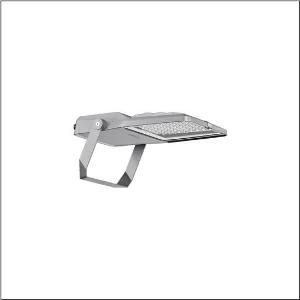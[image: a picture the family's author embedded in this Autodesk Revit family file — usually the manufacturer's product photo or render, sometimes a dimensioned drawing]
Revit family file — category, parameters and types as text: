
# Revit family: floodlight_fl_21_iq_mini___pl52_5xa7772c1d1a_38f0
name_source: partatom
category: Lighting Fixtures
units: mm (PartAtom-declared; Revit-internal decimal feet)

## family parameters
Cut with Voids When Loaded = No
Host = Face
Light Source = No
Part Type = Normal
Room Calculation Point = No
Round Connector Dimension = Use Diameter
Shared = No

## types (1)
- --- (1 x LED, 10110 lm, 87.2 W, 2200K)
    Apparent Load = 87 VA
    CIE Flux Codes = 26 60 98 100 100
    Color Rendering = 70
    Color Temperature = 2200K
    Default Elevation = 1800 mm
    Description = Floodlight FL 21 iQ mini, floodlight, primary light control with lens, of PMMA, primary optical cover: protective disc, of toughened safety glass, transparent, light distribution: PL52, light emission: direct distribution, installation type: surface-mounted, LED, High Power LED, rated luminous flux: 10.110lm, luminous efficacy: 116lm/W, light colour: 722, colour temperature: 2200K, control: Street-Remote, Auto-Match, Temp-Guard, Night-Set, Smart-Wire, Desk-Remote (wireless, voltage-free reading and setting of iQ features in the workshop via application-optimized NFC function/RFID function), optimised constant luminous flux control (CLO 2.0), with terminal, 6-pole, mains connection: 220..240V, AC, 50/60Hz, start of lifetime: 87W, end of service life: 92W, reduction: 40W, luminaire housing, of diecast aluminium, powder-coated, Siteco® metallic grey (DB 702S), corrosivity category C5 mid according to DIN EN ISO 12944, sealing non-destructively replaceable, mounting bracket, of steel, galvanised, powder-coated, Siteco® metallic grey (DB 702S), protection rating (complete): IP66, insulation class (complete): insulation class II (safety insulation), certification: CE, ENEC, VDE, protection symbol: D, impact resistance: IK08, permissible operating ambient temperature: -40..+40°C, permissible operating ambient temperature for outdoor applications: -40..+50°C, standard: DIN EN 12944, LABS conformity tested according to VDMA 24364:2018-05, packaging unit: 1 piece

Light Distribution: PL52
    Height = 70 mm
    Lamp = 1 x LED
    Lamp Light Flux = 10110 lm
    Lamp Power = 87.2 W
    Lamp count = 1
    Length = 485 mm
    Luminous efficacy = 116 lm/W
    Manufacturer = Siteco
    ModVariant = No
    Model = 5XA7772C1D1A
    Number of Poles = 1
    OnlyDefault = Yes
    Power Factor = 1
    Product Name = Floodlight FL 21 iQ mini | PL52
    Product group = floodlight | pylon annexe
    ProductGroupID = 6200
    Protection Class = Protection class II
    Protection Degree = IP 66
    RLX_Detail_Level = 1
    RLX_Emergency_Light_Flux = 0 lm
    RLX_Emergency_Type = 0
    RLX_Emergency_Type_DB = No
    RlxData = <blob elided: 96337 chars, md5=0ddbd2a6>
    Socket = socket
    Standby Power = 0 W
    System Light Flux = 10110 lm
    System Power = 87 W
    Type Comments = factory setting: luminous flux: 100 % | dim-lin: 254 | 456 mA
    Type Image = l_1006845.jpg
    URL = http://relux.com
    VarID = @adj_096711
    Voltage = 0 V
    Weight = 0.00 kg
    Width = 337 mm

## geometry (parser evidence)
native form markers: Blend x4, Sweep x15
no freeform markers — native parametric forms only
